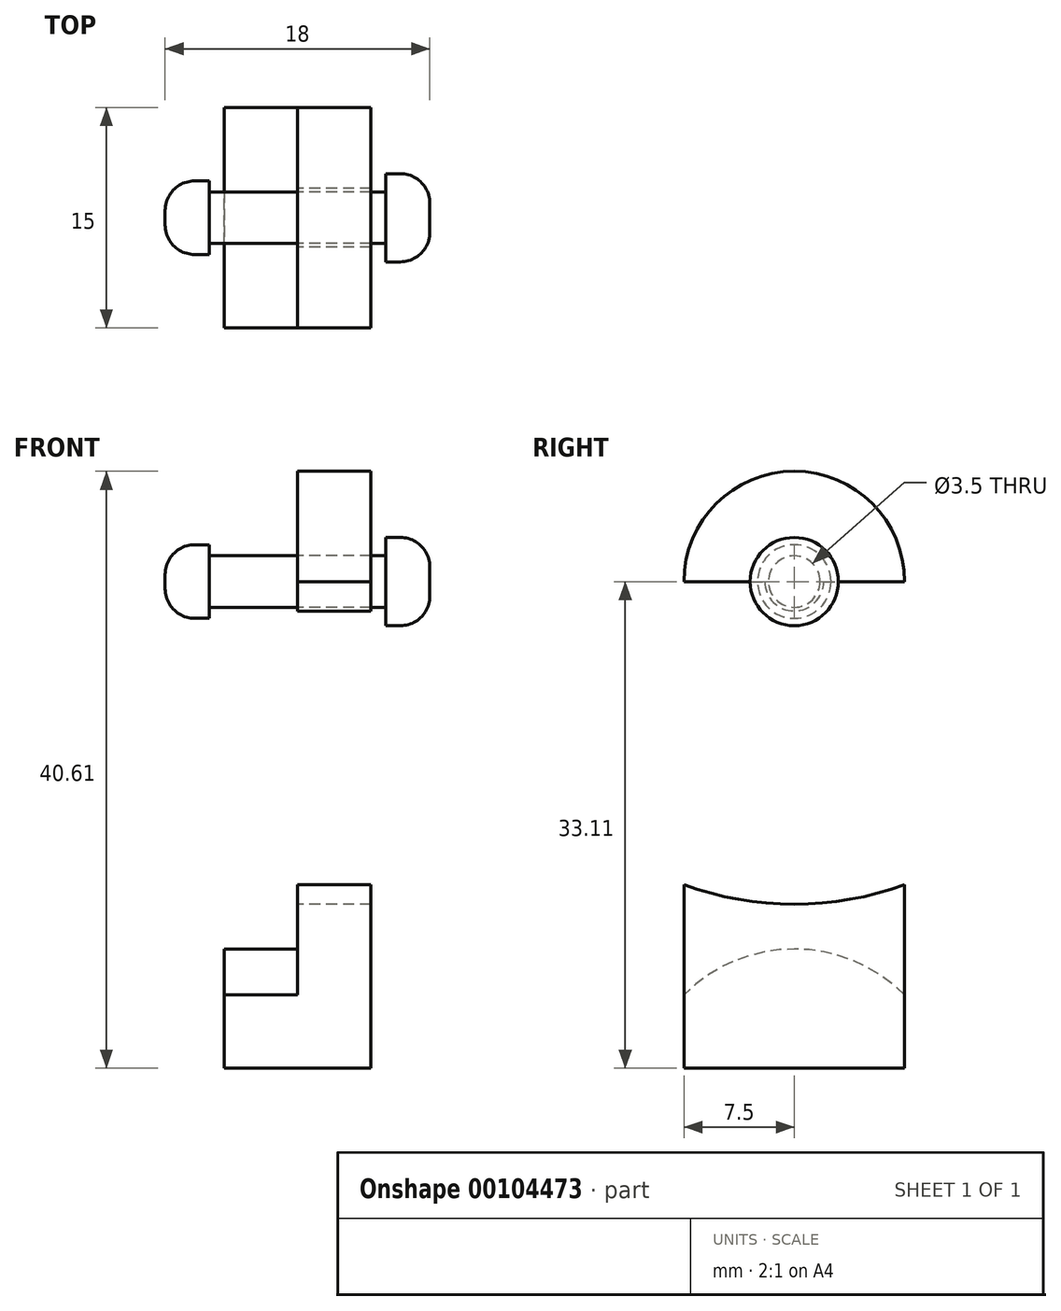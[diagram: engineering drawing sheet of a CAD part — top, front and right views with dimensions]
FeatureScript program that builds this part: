
annotation { "Feature Type Name" : "Feature", "Feature Type Description" : "" }
export const myFeature = defineFeature(function(context is Context, id is Id, definition is map)
    precondition{}
    {
        {
            var Q0;
            Q0=qCreatedBy(makeId("Right.planeOp"),FACE);
            var sketch = newSketch(context, id + "F0", { "sketchPlane" : qUnion([Q0])});
            skLineSegment(sketch, "E0.bottom", {"start": v(-7.5, -18.1) * mm, "end": v(7.5, -18.1) * mm});
            skLineSegment(sketch, "E0.top", {"start": v(-7.5, 15) * mm, "end": v(7.5, 15) * mm});
            skLineSegment(sketch, "E0.left", {"start": v(-7.5, -18.1) * mm, "end": v(-7.5, 15) * mm});
            skLineSegment(sketch, "E0.right", {"start": v(7.5, -18.1) * mm, "end": v(7.5, 15) * mm});
            skPoint(sketch, "E0.middle", {"position": v(0, 15) * mm});
            skLineSegment(sketch, "E1", {"start": v(7.5, -18.1) * mm, "end": v(7.5, -13.1) * mm});
            skArc(sketch, "E2", {"start": v(7.5, -13.1) * mm, "mid": v(0, -10) * mm, "end": v(-7.5, -13.1) * mm});
            skArc(sketch, "E3", {"start": v(-7.5, 15) * mm, "mid": v(0, 22.5) * mm, "end": v(7.5, 15) * mm});
            skCircle(sketch, "E4", {"center": v(0, 15) * mm, "radius": 2 * mm});
            skCircle(sketch, "E5", {"center": v(0, 15) * mm, "radius": 1.75 * mm});
            skCircle(sketch, "E6", {"center": v(0, 15) * mm, "radius": 1.95 * mm});
            skCircle(sketch, "E7.0", {"center": v(0, 15) * mm, "radius": 21.95 * mm});
            skSolve(sketch);
        }
        {
            var Q0;
            Q0=makeQuery(id+"F0.imprint","IMPRINT",FACE,{"disambiguationData":[TD([[makeQuery(id+"F0.imprint","IMPRINT",EDGE,{"derivedFrom":sQuery(id+"F0.wireOp",EDGE,"E0.top")}),1.0]])]});
            var Q1;
            {var subQ2=sQuery(id+"F0.wireOp",EDGE,"E0.top");Q1=makeQuery(id+"F0.imprint","IMPRINT",FACE,{"disambiguationData":[TD([[makeQuery(id+"F0.imprint","IMPRINT",EDGE,{"derivedFrom":subQ2}),-1.0]])]});}
            var Q2;
            {var subQ0=sQuery(id+"F0.wireOp",EDGE,"E2");Q2=makeQuery(id+"F0.imprint","IMPRINT",FACE,{"disambiguationData":[TD([[makeQuery(id+"F0.imprint","IMPRINT",EDGE,{"derivedFrom":subQ0}),-1.0]])]});}
            var Q3;
            {var subQ0=sQuery(id+"F0.wireOp",EDGE,"E0.bottom");Q3=makeQuery(id+"F0.imprint","IMPRINT",FACE,{"disambiguationData":[TD([[makeQuery(id+"F0.imprint","IMPRINT",EDGE,{"derivedFrom":subQ0}),1.0]])]});}
            var Q4;
            {var subQ2=sQuery(id+"F0.wireOp",EDGE,"E0.top");var subQ9=sQuery(id+"F0.wireOp",EDGE,"E4");var subQ11=makeQuery(id+"F0.imprint","INTERSECT",VERTEX,{"disambiguationData":[OD(0.0)],"derivedFrom":[subQ2,subQ9]});Q4=makeQuery(id+"F0.imprint","IMPRINT",FACE,{"disambiguationData":[TD([[makeQuery(id+"F0.imprint","IMPRINT",EDGE,{"disambiguationData":[TD([[subQ11,-1.0]])],"derivedFrom":subQ9}),-1.0]])]});}
            extrude(context, id + "F1", {"entities" : qUnion([Q0, Q1, Q2, Q3, Q4]), "depth" : 5 * mm});
        }
        {
            var Q0;
            {var subQ0=sQuery(id+"F0.wireOp",EDGE,"E0.bottom");Q0=makeQuery(id+"F0.imprint","IMPRINT",FACE,{"disambiguationData":[TD([[makeQuery(id+"F0.imprint","IMPRINT",EDGE,{"derivedFrom":subQ0}),1.0]])]});}
            extrude(context, id + "F2", {"entities" : qUnion([Q0]), "operationType" : NewBodyOperationType.ADD, "oppositeDirection" : true, "depth" : 5 * mm});
        }
        {
            var Q0;
            Q0=makeQuery(id+"F0.imprint","IMPRINT",FACE,{"disambiguationData":[TD([[makeQuery(id+"F0.imprint","IMPRINT",EDGE,{"derivedFrom":sQuery(id+"F0.wireOp",EDGE,"E5")}),1.0]])]});
            extrude(context, id + "F3", {"entities" : qUnion([Q0]), "depth" : 6 * mm});
        }
        {
            var Q0;
            Q0=makeQuery(id+"F3.opExtrude","CAP_FACE",FACE,{"disambiguationData":[OSD([sQuery(id+"F0.wireOp",EDGE,"E5")])],"isStart":false});
            var sketch = newSketch(context, id + "F4", { "sketchPlane" : qUnion([Q0])});
            skCircle(sketch, "E8", {"center": v(0, 15) * mm, "radius": 3 * mm});
            skLineSegment(sketch, "E9", {"start": v(0, 0) * mm, "end": v(0, 15) * mm});
            skLineSegment(sketch, "E10", {"start": v(0, 15) * mm, "end": v(-1.75, 15) * mm});
            skLineSegment(sketch, "E11", {"start": v(0, 15) * mm, "end": v(1.75, 15) * mm});
            skSolve(sketch);
        }
        {
            var Q0;
            Q0 = qSketchRegion(id + "F4", true);
            extrude(context, id + "F5", {"entities" : qUnion([Q0]), "operationType" : NewBodyOperationType.ADD, "depth" : 3 * mm});
        }
        {
            var Q0;
            Q0=makeQuery(id+"F5.opExtrude","CAP_EDGE",EDGE,{"disambiguationData":[OSD([sQuery(id+"F4.wireOp",EDGE,"E8")])],"isStart":false});
            fillet(context, id + "F6", {"entities" : qUnion([Q0]), "radius" : 2 * mm, "tangentPropagation" : true, "allowEdgeOverflow" : false});
        }
        {
            var Q0;
            Q0=makeQuery(id+"F0.imprint","IMPRINT",FACE,{"disambiguationData":[TD([[makeQuery(id+"F0.imprint","IMPRINT",EDGE,{"derivedFrom":sQuery(id+"F0.wireOp",EDGE,"E5")}),1.0]])]});
            var Q1;
            Q1 = qSketchRegion(id + "F8", true);
            var Q2;
            Q2=sQuery(id+"F0.wireOp",EDGE,"E5");
            extrude(context, id + "F7", {"entities" : qUnion([Q0, Q1]), "surfaceEntities" : qUnion([Q2]), "oppositeDirection" : true, "depth" : 6 * mm});
        }
        {
            var Q0;
            Q0=makeQuery(id+"F7.opExtrude","CAP_FACE",FACE,{"disambiguationData":[OSD([sQuery(id+"F0.wireOp",EDGE,"E5")])],"isStart":false});
            var sketch = newSketch(context, id + "F8", { "sketchPlane" : qUnion([Q0])});
            skCircle(sketch, "E12", {"center": v(0, 15) * mm, "radius": 2.5 * mm});
            skSolve(sketch);
        }
        {
            var Q0;
            Q0 = qSketchRegion(id + "F8", true);
            extrude(context, id + "F9", {"entities" : qUnion([Q0]), "operationType" : NewBodyOperationType.ADD, "depth" : 3 * mm});
        }
        {
            var Q0;
            Q0=makeQuery(id+"F9.opExtrude","CAP_EDGE",EDGE,{"disambiguationData":[OSD([sQuery(id+"F8.wireOp",EDGE,"E12")])],"isStart":false});
            fillet(context, id + "F10", {"entities" : qUnion([Q0]), "radius" : 2 * mm, "tangentPropagation" : true, "allowEdgeOverflow" : false});
        }
        {
            var Q0;
            Q0=sQuery(id+"F0.wireOp",EDGE,"E7.0");
            extrude(context, id + "F11", {"bodyType" : ToolBodyType.SURFACE, "surfaceEntities" : qUnion([Q0]), "oppositeDirection" : true, "depth" : 1 * mm});
        }
    });
